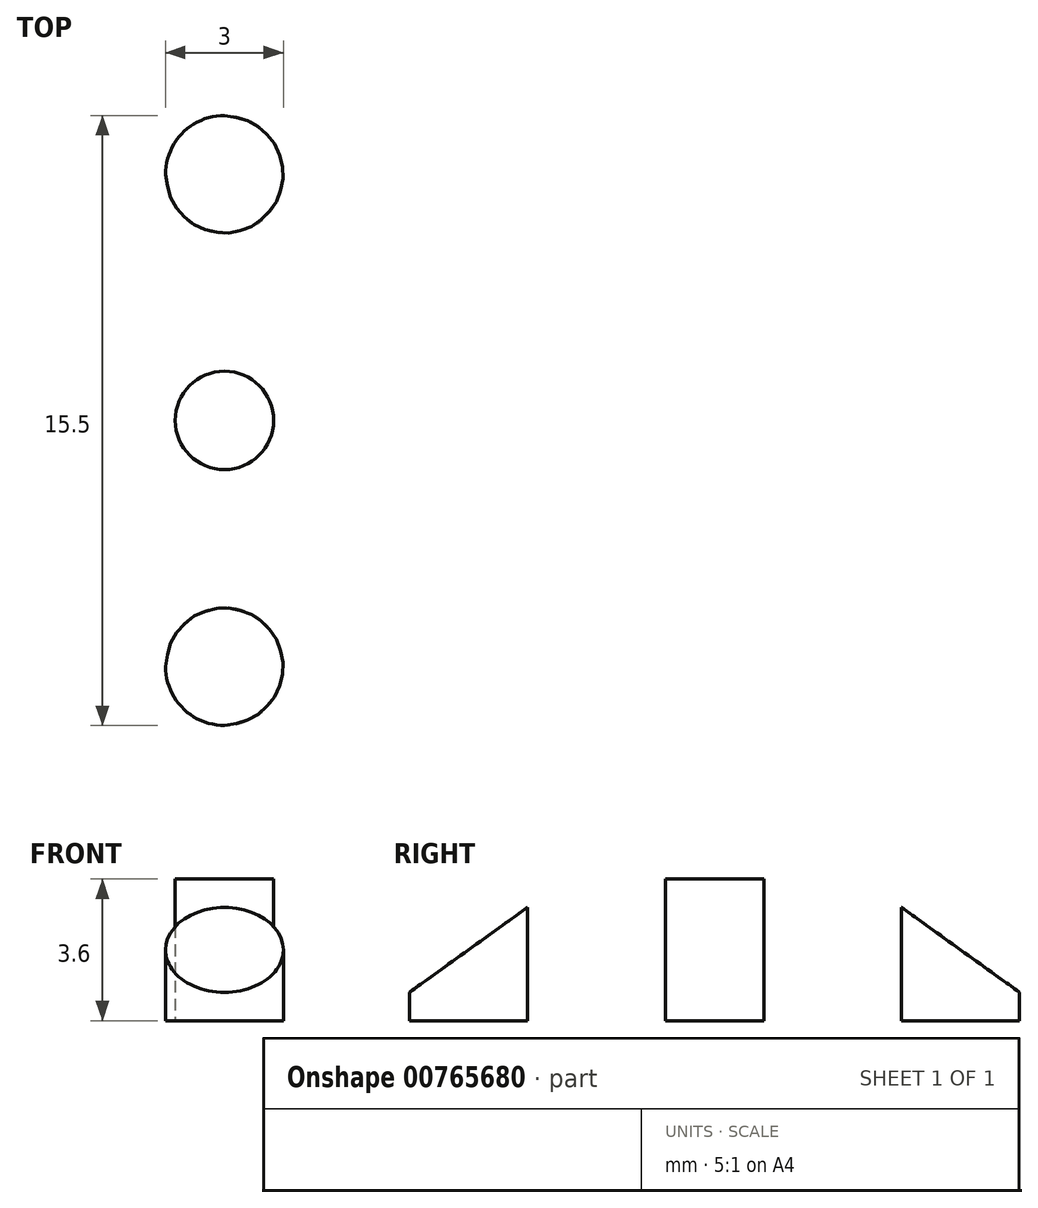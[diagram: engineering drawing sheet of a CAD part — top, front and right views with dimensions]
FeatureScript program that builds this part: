
annotation { "Feature Type Name" : "Feature", "Feature Type Description" : "" }
export const myFeature = defineFeature(function(context is Context, id is Id, definition is map)
    precondition{}
    {
        {
            var Q0;
            Q0=qCreatedBy(makeId("Front.planeOp"),FACE);
            var sketch = newSketch(context, id + "F0", { "sketchPlane" : qUnion([Q0])});
            skLineSegment(sketch, "E0.bottom", {"start": v(-16.9, 3.6) * mm, "end": v(16.9, 3.6) * mm});
            skLineSegment(sketch, "E0.top", {"start": v(-16.9, 0) * mm, "end": v(16.9, 0) * mm});
            skLineSegment(sketch, "E0.left", {"start": v(-16.9, 3.6) * mm, "end": v(-16.9, 0) * mm});
            skLineSegment(sketch, "E0.right", {"start": v(16.9, 3.6) * mm, "end": v(16.9, 0) * mm});
            skCircle(sketch, "E1", {"center": v(-9.3, 3.6) * mm, "radius": 2.6 * mm});
            skCircle(sketch, "E2", {"center": v(-3.1, 3.6) * mm, "radius": 2.6 * mm});
            skCircle(sketch, "E3", {"center": v(3.1, 3.6) * mm, "radius": 2.6 * mm});
            skCircle(sketch, "E4", {"center": v(9.3, 3.6) * mm, "radius": 2.6 * mm});
            skSolve(sketch);
        }
        {
            var Q0;
            Q0=makeQuery(id+"F0.imprint","IMPRINT",FACE,{"disambiguationData":[TD([[makeQuery(id+"F0.imprint","IMPRINT",EDGE,{"derivedFrom":sQuery(id+"F0.wireOp",EDGE,"E0.top")}),1.0]])]});
            extrude(context, id + "F1", {"entities" : qUnion([Q0]), "depth" : 7.5 * mm, "offsetDistance" : 25 * mm});
        }
        {
            var Q0;
            Q0=makeQuery(id+"F1.opExtrude","CAP_FACE",FACE,{"disambiguationData":[OSD([sQuery(id+"F0.wireOp",EDGE,"E0.bottom"),sQuery(id+"F0.wireOp",EDGE,"E0.top"),sQuery(id+"F0.wireOp",EDGE,"E0.left"),sQuery(id+"F0.wireOp",EDGE,"E0.right"),sQuery(id+"F0.wireOp",EDGE,"E1"),sQuery(id+"F0.wireOp",EDGE,"E2"),sQuery(id+"F0.wireOp",EDGE,"E3"),sQuery(id+"F0.wireOp",EDGE,"E4")])],"isStart":true});
            var sketch = newSketch(context, id + "F2", { "sketchPlane" : qUnion([Q0])});
            skLineSegment(sketch, "E5.bottom", {"start": v(-16.9, 0) * mm, "end": v(-11.9, 0) * mm});
            skLineSegment(sketch, "E5.top", {"start": v(-16.9, 3.6) * mm, "end": v(-11.9, 3.6) * mm});
            skLineSegment(sketch, "E5.left", {"start": v(-16.9, 0) * mm, "end": v(-16.9, 3.6) * mm});
            skLineSegment(sketch, "E5.right", {"start": v(-11.9, 0) * mm, "end": v(-11.9, 3.6) * mm});
            skLineSegment(sketch, "E6.bottom", {"start": v(16.9, 0) * mm, "end": v(11.9, 0) * mm});
            skLineSegment(sketch, "E6.top", {"start": v(16.9, 3.6) * mm, "end": v(11.9, 3.6) * mm});
            skLineSegment(sketch, "E6.left", {"start": v(16.9, 0) * mm, "end": v(16.9, 3.6) * mm});
            skLineSegment(sketch, "E6.right", {"start": v(11.9, 0) * mm, "end": v(11.9, 3.6) * mm});
            skSolve(sketch);
        }
        {
            var Q0;
            Q0 = qSketchRegion(id + "F2", true);
            extrude(context, id + "F3", {"entities" : qUnion([Q0]), "operationType" : NewBodyOperationType.ADD, "depth" : 5 * mm, "offsetDistance" : 25 * mm, "hasSecondDirection" : true, "secondDirectionOppositeDirection" : true, "secondDirectionDepth" : 12.5 * mm});
        }
        {
            var Q0;
            Q0=makeQuery(id+"F3.boolean.opBoolean","MERGE",FACE,{"derivedFrom":[makeQuery(id+"F1.opExtrude","SWEPT_FACE",FACE,{"disambiguationData":[OSD([sQuery(id+"F0.wireOp",EDGE,"E0.right")])]}),makeQuery(id+"F3.opExtrude","SWEPT_FACE",FACE,{"disambiguationData":[OSD([sQuery(id+"F2.wireOp",EDGE,"E5.left")])]})]});
            var sketch = newSketch(context, id + "F4", { "sketchPlane" : qUnion([Q0])});
            skLineSegment(sketch, "E7", {"start": v(-12.5, 3.6) * mm, "end": v(-7.5, 3.6) * mm});
            skLineSegment(sketch, "E8", {"start": v(-7.5, 3.6) * mm, "end": v(-12.5, 0) * mm});
            skLineSegment(sketch, "E9", {"start": v(-12.5, 0) * mm, "end": v(-12.5, 3.6) * mm});
            skLineSegment(sketch, "E10", {"start": v(5, 3.6) * mm, "end": v(0, 3.6) * mm});
            skLineSegment(sketch, "E11", {"start": v(0, 3.6) * mm, "end": v(5, 0) * mm});
            skLineSegment(sketch, "E12", {"start": v(5, 0) * mm, "end": v(5, 3.6) * mm});
            skSolve(sketch);
        }
        {
            var Q0;
            Q0 = qSketchRegion(id + "F4", true);
            extrude(context, id + "F5", {"entities" : qUnion([Q0]), "operationType" : NewBodyOperationType.REMOVE, "oppositeDirection" : true, "depth" : 35.2 * mm, "offsetDistance" : 25 * mm});
        }
        {
            var Q0;
            Q0=makeQuery(id+"F3.boolean.opBoolean","MERGE",FACE,{"derivedFrom":[makeQuery(id+"F1.opExtrude","SWEPT_FACE",FACE,{"disambiguationData":[OSD([sQuery(id+"F0.wireOp",EDGE,"E0.top")])]}),makeQuery(id+"F3.opExtrude","SWEPT_FACE",FACE,{"disambiguationData":[OSD([sQuery(id+"F2.wireOp",EDGE,"E5.bottom")])]}),makeQuery(id+"F3.opExtrude","SWEPT_FACE",FACE,{"disambiguationData":[OSD([sQuery(id+"F2.wireOp",EDGE,"E6.bottom")])]})]});
            var sketch = newSketch(context, id + "F6", { "sketchPlane" : qUnion([Q0])});
            skLineSegment(sketch, "E13", {"start": v(11.9, 7.5) * mm, "end": v(16.9, 12.5) * mm, "construction": true});
            skLineSegment(sketch, "E14", {"start": v(11.9, 0) * mm, "end": v(16.9, -5) * mm, "construction": true});
            skLineSegment(sketch, "E15", {"start": v(11.9, -5) * mm, "end": v(16.9, 0) * mm, "construction": true});
            skLineSegment(sketch, "E16", {"start": v(11.9, 12.5) * mm, "end": v(16.9, 7.5) * mm, "construction": true});
            skCircle(sketch, "E17", {"center": v(14.4, 10) * mm, "radius": 1.5 * mm});
            skCircle(sketch, "E18", {"center": v(14.4, -2.5) * mm, "radius": 1.5 * mm});
            skLineSegment(sketch, "E19", {"start": v(16.9, 7.5) * mm, "end": v(11.9, 0) * mm, "construction": true});
            skCircle(sketch, "E20", {"center": v(14.4, 3.75) * mm, "radius": 1.25 * mm});
            skLineSegment(sketch, "E21", {"start": v(0, 0) * mm, "end": v(0, 7.5) * mm, "construction": true});
            skCircle(sketch, "E22.MirrorC", {"center": v(-14.4, 10) * mm, "radius": 1.5 * mm});
            skCircle(sketch, "E23.MirrorC", {"center": v(-14.4, 3.75) * mm, "radius": 1.25 * mm});
            skCircle(sketch, "E24.MirrorC", {"center": v(-14.4, -2.5) * mm, "radius": 1.5 * mm});
            skSolve(sketch);
        }
        {
            var Q0;
            Q0=makeQuery(id+"F6.imprint","IMPRINT",FACE,{"disambiguationData":[TD([[makeQuery(id+"F6.imprint","IMPRINT",EDGE,{"derivedFrom":sQuery(id+"F6.wireOp",EDGE,"E17")}),1.0]])]});
            var Q1;
            Q1=makeQuery(id+"F6.imprint","IMPRINT",FACE,{"disambiguationData":[TD([[makeQuery(id+"F6.imprint","IMPRINT",EDGE,{"derivedFrom":sQuery(id+"F6.wireOp",EDGE,"E20")}),1.0]])]});
            var Q2;
            Q2=makeQuery(id+"F6.imprint","IMPRINT",FACE,{"disambiguationData":[TD([[makeQuery(id+"F6.imprint","IMPRINT",EDGE,{"derivedFrom":sQuery(id+"F6.wireOp",EDGE,"E18")}),1.0]])]});
            var Q3;
            Q3=makeQuery(id+"F6.imprint","IMPRINT",FACE,{"disambiguationData":[TD([[makeQuery(id+"F6.imprint","IMPRINT",EDGE,{"derivedFrom":sQuery(id+"F6.wireOp",EDGE,"E24.MirrorC")}),-1.0]])]});
            var Q4;
            Q4=makeQuery(id+"F6.imprint","IMPRINT",FACE,{"disambiguationData":[TD([[makeQuery(id+"F6.imprint","IMPRINT",EDGE,{"derivedFrom":sQuery(id+"F6.wireOp",EDGE,"E22.MirrorC")}),-1.0]])]});
            var Q5;
            Q5=makeQuery(id+"F6.imprint","IMPRINT",FACE,{"disambiguationData":[TD([[makeQuery(id+"F6.imprint","IMPRINT",EDGE,{"derivedFrom":sQuery(id+"F6.wireOp",EDGE,"E23.MirrorC")}),-1.0]])]});
            extrude(context, id + "F7", {"entities" : qUnion([Q0, Q1, Q2, Q3, Q4, Q5]), "operationType" : NewBodyOperationType.REMOVE, "oppositeDirection" : true, "depth" : 25 * mm, "offsetDistance" : 25 * mm});
        }
    });
